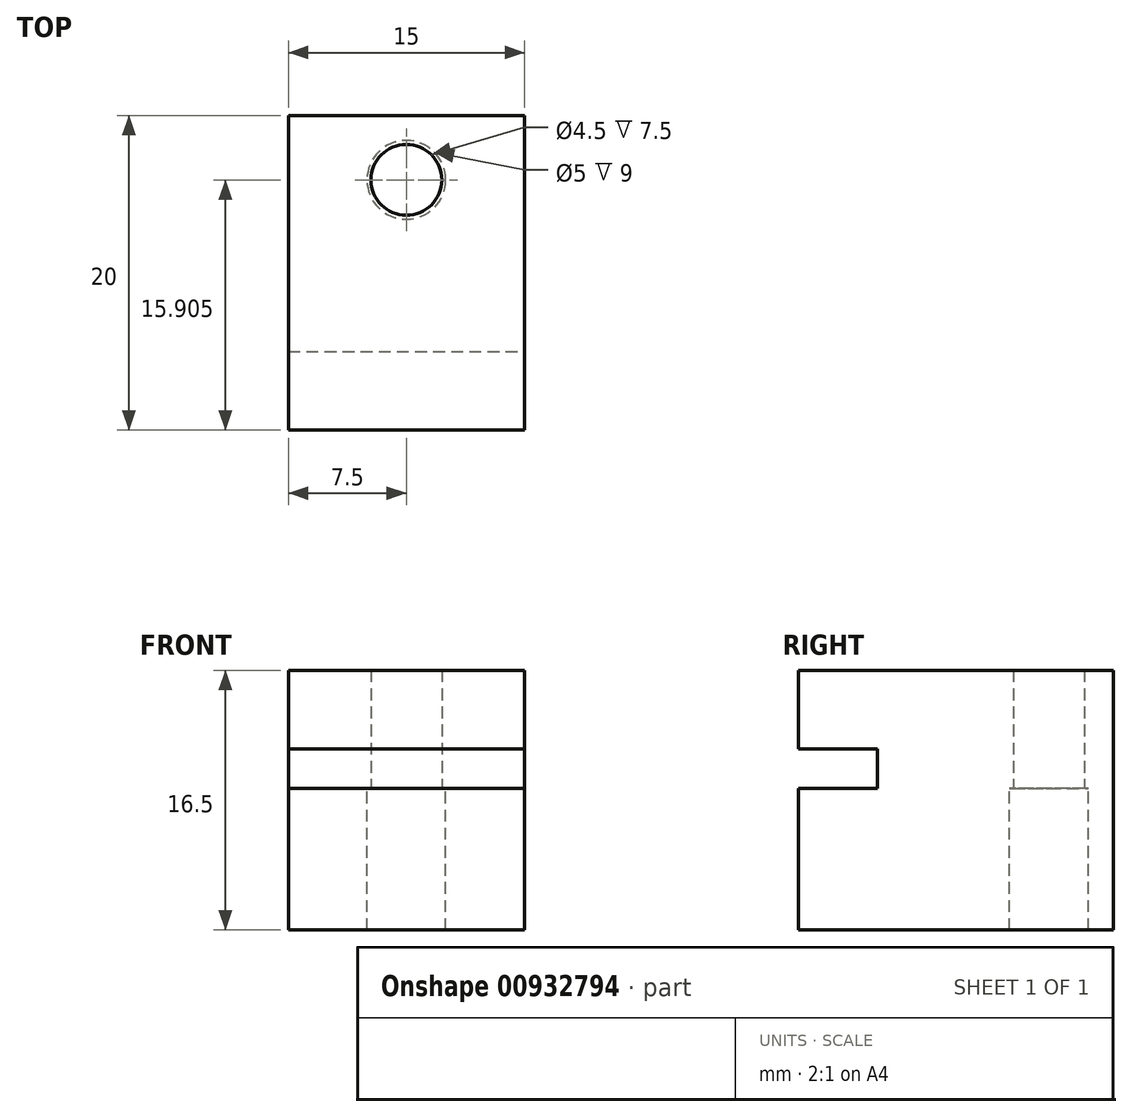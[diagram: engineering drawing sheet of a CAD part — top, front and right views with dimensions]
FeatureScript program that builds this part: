
annotation { "Feature Type Name" : "Feature", "Feature Type Description" : "" }
export const myFeature = defineFeature(function(context is Context, id is Id, definition is map)
    precondition{}
    {
        {
            var Q0;
            Q0=qCreatedBy(makeId("Top.planeOp"),FACE);
            var sketch = newSketch(context, id + "F0", { "sketchPlane" : qUnion([Q0])});
            skLineSegment(sketch, "E0.bottom", {"start": v(0, 0) * mm, "end": v(15, 0) * mm});
            skLineSegment(sketch, "E0.top", {"start": v(0, 15) * mm, "end": v(15, 15) * mm});
            skLineSegment(sketch, "E0.left", {"start": v(0, 0) * mm, "end": v(0, 15) * mm});
            skLineSegment(sketch, "E0.right", {"start": v(15, 0) * mm, "end": v(15, 15) * mm});
            skCircle(sketch, "E1", {"center": v(7.5, 10.9) * mm, "radius": 2.25 * mm});
            skSolve(sketch);
        }
        {
            var Q0;
            Q0 = qSketchRegion(id + "F0", true);
            extrude(context, id + "F1", {"entities" : qUnion([Q0]), "depth" : 2.5 * mm, "offsetDistance" : 25 * mm});
        }
        {
            var Q0;
            Q0=makeQuery(id+"F1.opExtrude","CAP_FACE",FACE,{"disambiguationData":[OSD([sQuery(id+"F0.wireOp",EDGE,"E0.bottom"),sQuery(id+"F0.wireOp",EDGE,"E0.top"),sQuery(id+"F0.wireOp",EDGE,"E0.left"),sQuery(id+"F0.wireOp",EDGE,"E0.right"),sQuery(id+"F0.wireOp",EDGE,"E1")])],"isStart":false});
            var sketch = newSketch(context, id + "F2", { "sketchPlane" : qUnion([Q0])});
            skLineSegment(sketch, "E2.bottom", {"start": v(0, 15) * mm, "end": v(15, 15) * mm});
            skLineSegment(sketch, "E2.top", {"start": v(0, -5) * mm, "end": v(15, -5) * mm});
            skLineSegment(sketch, "E2.left", {"start": v(0, 15) * mm, "end": v(0, -5) * mm});
            skLineSegment(sketch, "E2.right", {"start": v(15, 15) * mm, "end": v(15, -5) * mm});
            skCircle(sketch, "E3", {"center": v(7.5, 10.9) * mm, "radius": 2.25 * mm});
            skSolve(sketch);
        }
        {
            var Q0;
            Q0 = qSketchRegion(id + "F2", true);
            extrude(context, id + "F3", {"entities" : qUnion([Q0]), "operationType" : NewBodyOperationType.ADD, "depth" : 5 * mm, "offsetDistance" : 25 * mm});
        }
        {
            var Q0;
            Q0=makeQuery(id+"F1.opExtrude","CAP_FACE",FACE,{"disambiguationData":[OSD([sQuery(id+"F0.wireOp",EDGE,"E0.bottom"),sQuery(id+"F0.wireOp",EDGE,"E0.top"),sQuery(id+"F0.wireOp",EDGE,"E0.left"),sQuery(id+"F0.wireOp",EDGE,"E0.right"),sQuery(id+"F0.wireOp",EDGE,"E1")])],"isStart":true});
            var sketch = newSketch(context, id + "F4", { "sketchPlane" : qUnion([Q0])});
            skLineSegment(sketch, "E4.bottom", {"start": v(0, -15) * mm, "end": v(15, -15) * mm});
            skLineSegment(sketch, "E4.top", {"start": v(0, 5) * mm, "end": v(15, 5) * mm});
            skLineSegment(sketch, "E4.left", {"start": v(0, -15) * mm, "end": v(0, 5) * mm});
            skLineSegment(sketch, "E4.right", {"start": v(15, -15) * mm, "end": v(15, 5) * mm});
            skCircle(sketch, "E5", {"center": v(7.5, -10.9) * mm, "radius": 2.5 * mm});
            skSolve(sketch);
        }
        {
            var Q0;
            Q0 = qSketchRegion(id + "F4", true);
            extrude(context, id + "F5", {"entities" : qUnion([Q0]), "operationType" : NewBodyOperationType.ADD, "depth" : 9 * mm, "offsetDistance" : 25 * mm});
        }
    });
